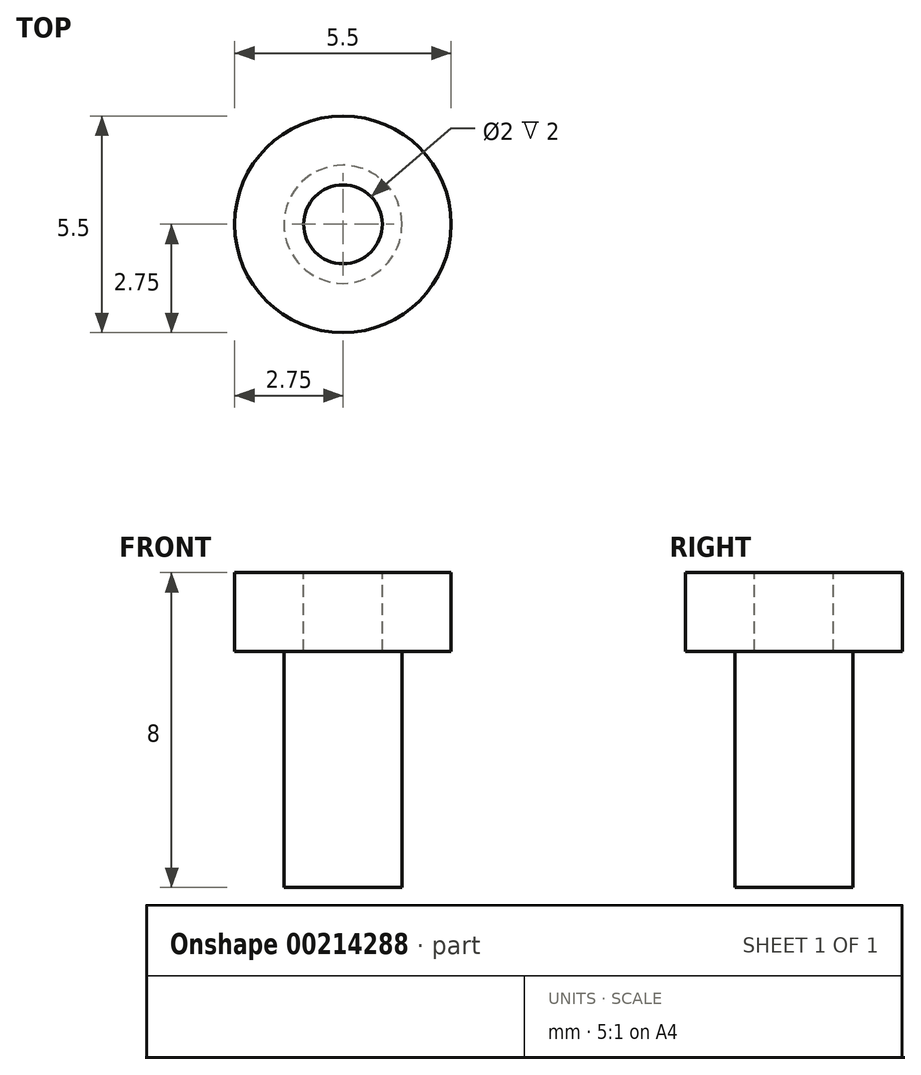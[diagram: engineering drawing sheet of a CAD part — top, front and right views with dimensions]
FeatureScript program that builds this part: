
annotation { "Feature Type Name" : "Feature", "Feature Type Description" : "" }
export const myFeature = defineFeature(function(context is Context, id is Id, definition is map)
    precondition{}
    {
        {
            var Q0;
            Q0=qCreatedBy(makeId("Top.planeOp"),FACE);
            var sketch = newSketch(context, id + "F0", { "sketchPlane" : qUnion([Q0])});
            skCircle(sketch, "E0", {"center": v(0, 0) * mm, "radius": 2.75 * mm});
            skSolve(sketch);
        }
        {
            var Q0;
            Q0 = qSketchRegion(id + "F0", true);
            extrude(context, id + "F1", {"entities" : qUnion([Q0]), "depth" : 8 * mm});
        }
        {
            var Q0;
            Q0=makeQuery(id+"F1.opExtrude","CAP_FACE",FACE,{"disambiguationData":[OSD([sQuery(id+"F0.wireOp",EDGE,"E0")])],"isStart":true});
            var sketch = newSketch(context, id + "F2", { "sketchPlane" : qUnion([Q0])});
            skCircle(sketch, "E1", {"center": v(0, 0) * mm, "radius": 1.5 * mm});
            skCircle(sketch, "E2", {"center": v(0, 0) * mm, "radius": 2.75 * mm});
            skSolve(sketch);
        }
        {
            var Q0;
            Q0 = qSketchRegion(id + "F2", true);
            extrude(context, id + "F3", {"entities" : qUnion([Q0]), "operationType" : NewBodyOperationType.REMOVE, "oppositeDirection" : true, "depth" : 6 * mm});
        }
        {
            var Q0;
            Q0=makeQuery(id+"F1.opExtrude","CAP_FACE",FACE,{"disambiguationData":[OSD([sQuery(id+"F0.wireOp",EDGE,"E0")])],"isStart":false});
            var sketch = newSketch(context, id + "F4", { "sketchPlane" : qUnion([Q0])});
            skCircle(sketch, "E3", {"center": v(0, 0) * mm, "radius": 1 * mm});
            skSolve(sketch);
        }
        {
            var Q0;
            Q0 = qSketchRegion(id + "F4", true);
            extrude(context, id + "F5", {"entities" : qUnion([Q0]), "operationType" : NewBodyOperationType.REMOVE, "oppositeDirection" : true, "depth" : 2 * mm});
        }
    });
